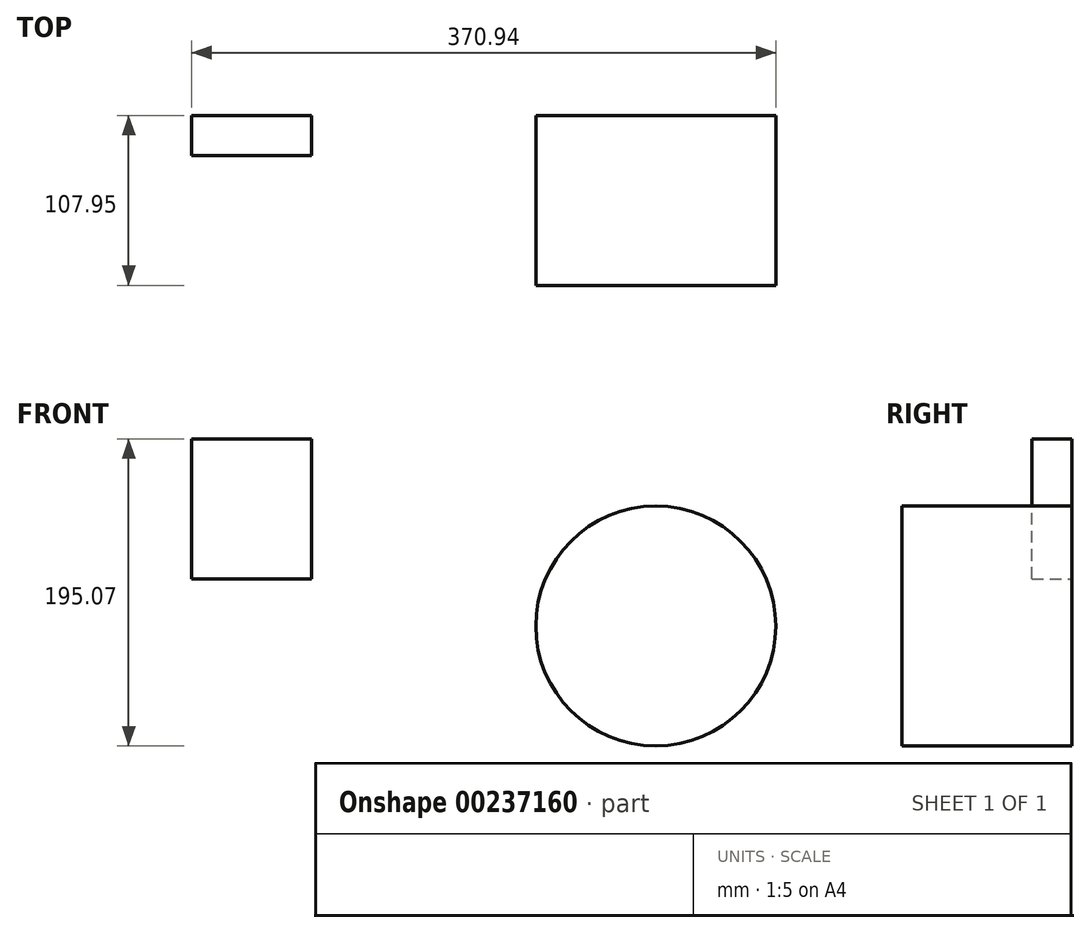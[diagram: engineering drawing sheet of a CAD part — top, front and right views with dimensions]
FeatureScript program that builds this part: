
annotation { "Feature Type Name" : "Feature", "Feature Type Description" : "" }
export const myFeature = defineFeature(function(context is Context, id is Id, definition is map)
    precondition{}
    {
        {
            var Q0;
            Q0=qCreatedBy(makeId("Front.planeOp"),FACE);
            var sketch = newSketch(context, id + "F0", { "sketchPlane" : qUnion([Q0])});
            skCircle(sketch, "E0", {"center": v(49.55, -50.9) * mm, "radius": 76.2 * mm});
            skSolve(sketch);
        }
        {
            var Q0;
            Q0 = qSketchRegion(id + "F0", true);
            extrude(context, id + "F1", {"entities" : qUnion([Q0]), "depth" : 107.95 * mm});
        }
        {
            var Q0;
            Q0=qCreatedBy(makeId("Front.planeOp"),FACE);
            var sketch = newSketch(context, id + "F2", { "sketchPlane" : qUnion([Q0])});
            skLineSegment(sketch, "E1.bottom", {"start": v(-169, -20.93) * mm, "end": v(-245.2, -20.93) * mm});
            skLineSegment(sketch, "E1.top", {"start": v(-169, 67.97) * mm, "end": v(-245.2, 67.97) * mm});
            skLineSegment(sketch, "E1.left", {"start": v(-169, -20.93) * mm, "end": v(-169, 67.97) * mm});
            skLineSegment(sketch, "E1.right", {"start": v(-245.2, -20.93) * mm, "end": v(-245.2, 67.97) * mm});
            skSolve(sketch);
        }
        {
            var Q0;
            Q0 = qSketchRegion(id + "F2", true);
            extrude(context, id + "F3", {"entities" : qUnion([Q0]), "depth" : 25.4 * mm});
        }
    });
